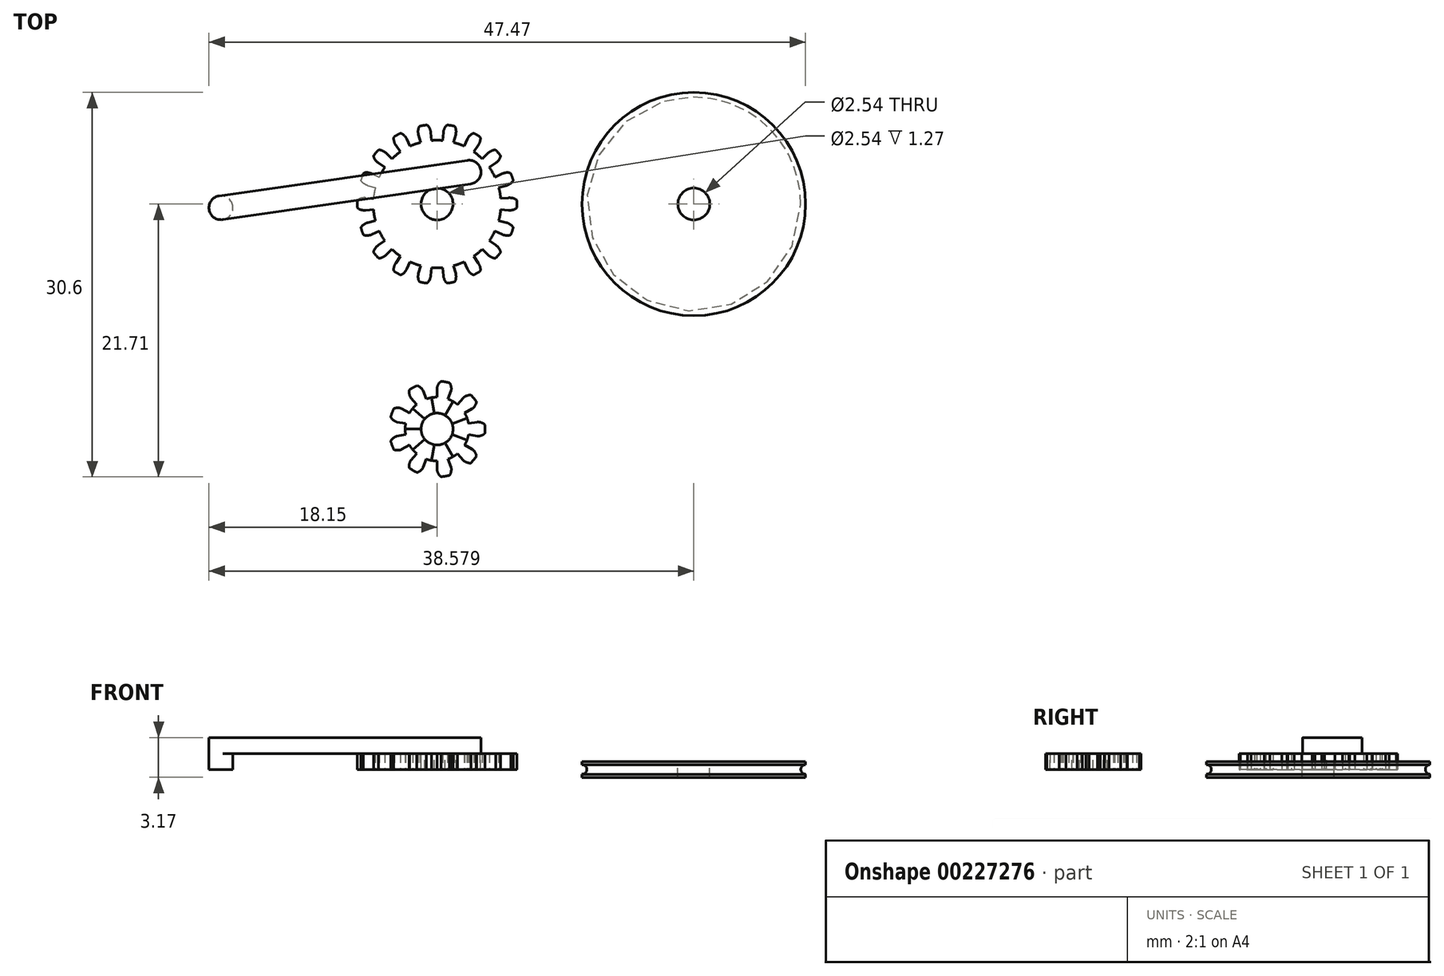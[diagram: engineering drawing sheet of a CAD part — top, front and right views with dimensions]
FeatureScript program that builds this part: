
annotation { "Feature Type Name" : "Feature", "Feature Type Description" : "" }
export const myFeature = defineFeature(function(context is Context, id is Id, definition is map)
    precondition{}
    {
        {
            var Q0;
            Q0=qCreatedBy(makeId("Top.planeOp"),FACE);
            var sketch = newSketch(context, id + "F0", { "sketchPlane" : qUnion([Q0])});
            skCircle(sketch, "E0", {"center": v(0, 0) * mm, "radius": 6.35 * mm, "construction": true});
            skCircle(sketch, "E1", {"center": v(0, 0) * mm, "radius": 5.72 * mm, "construction": true});
            skCircle(sketch, "E2", {"center": v(0, 0) * mm, "radius": 5.08 * mm, "construction": true});
            skLineSegment(sketch, "E3", {"start": v(0, 0) * mm, "end": v(7.72, 0) * mm, "construction": true});
            skLineSegment(sketch, "E4", {"start": v(0, 0) * mm, "end": v(7.94, 1.4) * mm, "construction": true});
            skLineSegment(sketch, "E5", {"start": v(0, 0) * mm, "end": v(7.47, 0.65) * mm, "construction": true});
            skLineSegment(sketch, "E6", {"start": v(0, 0) * mm, "end": v(7.02, 0.3) * mm, "construction": true});
            skFitSpline(sketch, "E7", {"points": [v(5.7, 0.5) * mm, v(6.34, 0.28) * mm], "startDerivative": vector(0.82, 0.07) * mm, "endDerivative": vector(0.13, -0.38) * mm});
            skLineSegment(sketch, "E8", {"start": v(5.7, 0.5) * mm, "end": v(5.06, 0.44) * mm});
            skPoint(sketch, "E9", {"position": v(5, 0.88) * mm});
            skArc(sketch, "E10", {"start": v(5.06, 0.44) * mm, "mid": v(5.04, 0.66) * mm, "end": v(5, 0.88) * mm});
            skArc(sketch, "E11", {"start": v(6.35, 0) * mm, "mid": v(6.35, 0.14) * mm, "end": v(6.34, 0.28) * mm});
            skPoint(sketch, "E12", {"position": v(6.35, 0) * mm});
            skLineSegment(sketch, "E13.MirrorCS", {"start": v(0, 0) * mm, "end": v(5, -0.88) * mm});
            skArc(sketch, "E14.MirrorCS", {"start": v(5.06, -0.44) * mm, "mid": v(5.04, -0.66) * mm, "end": v(5, -0.88) * mm});
            skLineSegment(sketch, "E15.MirrorCS", {"start": v(5.7, -0.5) * mm, "end": v(5.06, -0.44) * mm});
            skFitSpline(sketch, "E16.MirrorCS", {"points": [v(5.7, -0.5) * mm, v(6.34, -0.28) * mm], "startDerivative": vector(0.82, -0.07) * mm, "endDerivative": vector(0.13, 0.38) * mm});
            skArc(sketch, "E17.MirrorCS", {"start": v(6.35, 0) * mm, "mid": v(6.35, -0.14) * mm, "end": v(6.34, -0.28) * mm});
            skLineSegment(sketch, "E18", {"start": v(0, 0) * mm, "end": v(5, 0.88) * mm});
            skSolve(sketch);
        }
        {
            var Q0;
            Q0=makeQuery(id+"F0.imprint","IMPRINT",FACE,{"disambiguationData":[TD([[makeQuery(id+"F0.imprint","IMPRINT",EDGE,{"derivedFrom":sQuery(id+"F0.wireOp",EDGE,"E7")}),-1.0]])]});
            extrude(context, id + "F1", {"entities" : qUnion([Q0]), "depth" : 1.27 * mm});
        }
        {
            var Q0;
            Q0=makeQuery(id+"F1.opExtrude","SWEPT_BODY",BODY,{"disambiguationData":[OSD([sQuery(id+"F0.wireOp",EDGE,"E7"),sQuery(id+"F0.wireOp",EDGE,"E8"),sQuery(id+"F0.wireOp",EDGE,"E10"),sQuery(id+"F0.wireOp",EDGE,"E11"),sQuery(id+"F0.wireOp",EDGE,"E13.MirrorCS"),sQuery(id+"F0.wireOp",EDGE,"E14.MirrorCS"),sQuery(id+"F0.wireOp",EDGE,"E15.MirrorCS"),sQuery(id+"F0.wireOp",EDGE,"E16.MirrorCS"),sQuery(id+"F0.wireOp",EDGE,"E17.MirrorCS"),sQuery(id+"F0.wireOp",EDGE,"E18")])]});
            var Q1;
            Q1=makeQuery(id+"F1.opExtrude","SWEPT_EDGE",EDGE,{"disambiguationData":[OSD([sQuery(id+"F0.wireOp",EDGE,"E13.MirrorCS"),sQuery(id+"F0.wireOp",EDGE,"E18")])]});
            circularPattern(context, id + "F2", {"operationType" : NewBodyOperationType.ADD, "entities" : qUnion([Q0]), "axis" : qUnion([Q1]), "angle" : 360 * degree, "instanceCount" : 18, "equalSpace" : true});
        }
        {
            var Q0;
            {var subQ0=makeQuery(id+"F1.opExtrude","CAP_FACE",FACE,{"disambiguationData":[OSD([sQuery(id+"F0.wireOp",EDGE,"E7"),sQuery(id+"F0.wireOp",EDGE,"E8"),sQuery(id+"F0.wireOp",EDGE,"E10"),sQuery(id+"F0.wireOp",EDGE,"E11"),sQuery(id+"F0.wireOp",EDGE,"E13.MirrorCS"),sQuery(id+"F0.wireOp",EDGE,"E14.MirrorCS"),sQuery(id+"F0.wireOp",EDGE,"E15.MirrorCS"),sQuery(id+"F0.wireOp",EDGE,"E16.MirrorCS"),sQuery(id+"F0.wireOp",EDGE,"E17.MirrorCS"),sQuery(id+"F0.wireOp",EDGE,"E18")])],"isStart":false});Q0=makeQuery(id+"F2.boolean.opBoolean","MERGE",FACE,{"derivedFrom":[subQ0,makeQuery(id+"F2.opPattern","COPY",FACE,{"derivedFrom":subQ0,"instanceName":"1"}),makeQuery(id+"F2.opPattern","COPY",FACE,{"derivedFrom":subQ0,"instanceName":"2"}),makeQuery(id+"F2.opPattern","COPY",FACE,{"derivedFrom":subQ0,"instanceName":"3"}),makeQuery(id+"F2.opPattern","COPY",FACE,{"derivedFrom":subQ0,"instanceName":"4"}),makeQuery(id+"F2.opPattern","COPY",FACE,{"derivedFrom":subQ0,"instanceName":"5"}),makeQuery(id+"F2.opPattern","COPY",FACE,{"derivedFrom":subQ0,"instanceName":"6"}),makeQuery(id+"F2.opPattern","COPY",FACE,{"derivedFrom":subQ0,"instanceName":"7"}),makeQuery(id+"F2.opPattern","COPY",FACE,{"derivedFrom":subQ0,"instanceName":"8"}),makeQuery(id+"F2.opPattern","COPY",FACE,{"derivedFrom":subQ0,"instanceName":"9"}),makeQuery(id+"F2.opPattern","COPY",FACE,{"derivedFrom":subQ0,"instanceName":"10"}),makeQuery(id+"F2.opPattern","COPY",FACE,{"derivedFrom":subQ0,"instanceName":"11"}),makeQuery(id+"F2.opPattern","COPY",FACE,{"derivedFrom":subQ0,"instanceName":"12"}),makeQuery(id+"F2.opPattern","COPY",FACE,{"derivedFrom":subQ0,"instanceName":"13"}),makeQuery(id+"F2.opPattern","COPY",FACE,{"derivedFrom":subQ0,"instanceName":"14"}),makeQuery(id+"F2.opPattern","COPY",FACE,{"derivedFrom":subQ0,"instanceName":"15"}),makeQuery(id+"F2.opPattern","COPY",FACE,{"derivedFrom":subQ0,"instanceName":"16"}),makeQuery(id+"F2.opPattern","COPY",FACE,{"derivedFrom":subQ0,"instanceName":"17"})]});}
            var sketch = newSketch(context, id + "F3", { "sketchPlane" : qUnion([Q0])});
            skCircle(sketch, "E19", {"center": v(2.54, 2.54) * mm, "radius": 0.95 * mm});
            skPoint(sketch, "E20.0", {"position": v(0, 0) * mm});
            skSolve(sketch);
        }
        {
            var Q0;
            Q0=makeQuery(id+"F3.imprint","IMPRINT",FACE,{"disambiguationData":[TD([[makeQuery(id+"F3.imprint","IMPRINT",EDGE,{"derivedFrom":sQuery(id+"F3.wireOp",EDGE,"E19")}),1.0]])]});
            extrude(context, id + "F4", {"entities" : qUnion([Q0]), "operationType" : NewBodyOperationType.REMOVE, "oppositeDirection" : true, "depth" : 25.4 * mm});
        }
        {
            var Q0;
            {var subQ0=makeQuery(id+"F1.opExtrude","CAP_FACE",FACE,{"disambiguationData":[OSD([sQuery(id+"F0.wireOp",EDGE,"E7"),sQuery(id+"F0.wireOp",EDGE,"E8"),sQuery(id+"F0.wireOp",EDGE,"E10"),sQuery(id+"F0.wireOp",EDGE,"E11"),sQuery(id+"F0.wireOp",EDGE,"E13.MirrorCS"),sQuery(id+"F0.wireOp",EDGE,"E14.MirrorCS"),sQuery(id+"F0.wireOp",EDGE,"E15.MirrorCS"),sQuery(id+"F0.wireOp",EDGE,"E16.MirrorCS"),sQuery(id+"F0.wireOp",EDGE,"E17.MirrorCS"),sQuery(id+"F0.wireOp",EDGE,"E18")])],"isStart":false});Q0=makeQuery(id+"F2.boolean.opBoolean","MERGE",FACE,{"derivedFrom":[subQ0,makeQuery(id+"F2.opPattern","COPY",FACE,{"derivedFrom":subQ0,"instanceName":"1"}),makeQuery(id+"F2.opPattern","COPY",FACE,{"derivedFrom":subQ0,"instanceName":"2"}),makeQuery(id+"F2.opPattern","COPY",FACE,{"derivedFrom":subQ0,"instanceName":"3"}),makeQuery(id+"F2.opPattern","COPY",FACE,{"derivedFrom":subQ0,"instanceName":"4"}),makeQuery(id+"F2.opPattern","COPY",FACE,{"derivedFrom":subQ0,"instanceName":"5"}),makeQuery(id+"F2.opPattern","COPY",FACE,{"derivedFrom":subQ0,"instanceName":"6"}),makeQuery(id+"F2.opPattern","COPY",FACE,{"derivedFrom":subQ0,"instanceName":"7"}),makeQuery(id+"F2.opPattern","COPY",FACE,{"derivedFrom":subQ0,"instanceName":"8"}),makeQuery(id+"F2.opPattern","COPY",FACE,{"derivedFrom":subQ0,"instanceName":"9"}),makeQuery(id+"F2.opPattern","COPY",FACE,{"derivedFrom":subQ0,"instanceName":"10"}),makeQuery(id+"F2.opPattern","COPY",FACE,{"derivedFrom":subQ0,"instanceName":"11"}),makeQuery(id+"F2.opPattern","COPY",FACE,{"derivedFrom":subQ0,"instanceName":"12"}),makeQuery(id+"F2.opPattern","COPY",FACE,{"derivedFrom":subQ0,"instanceName":"13"}),makeQuery(id+"F2.opPattern","COPY",FACE,{"derivedFrom":subQ0,"instanceName":"14"}),makeQuery(id+"F2.opPattern","COPY",FACE,{"derivedFrom":subQ0,"instanceName":"15"}),makeQuery(id+"F2.opPattern","COPY",FACE,{"derivedFrom":subQ0,"instanceName":"16"}),makeQuery(id+"F2.opPattern","COPY",FACE,{"derivedFrom":subQ0,"instanceName":"17"})]});}
            var sketch = newSketch(context, id + "F5", { "sketchPlane" : qUnion([Q0])});
            skPoint(sketch, "E21.0", {"position": v(0, 0) * mm});
            skCircle(sketch, "E22", {"center": v(0, 0) * mm, "radius": 1.27 * mm});
            skSolve(sketch);
        }
        {
            var Q0;
            Q0=makeQuery(id+"F5.imprint","IMPRINT",FACE,{"disambiguationData":[TD([[makeQuery(id+"F5.imprint","IMPRINT",EDGE,{"derivedFrom":sQuery(id+"F5.wireOp",EDGE,"E22")}),1.0]])]});
            extrude(context, id + "F6", {"entities" : qUnion([Q0]), "operationType" : NewBodyOperationType.REMOVE, "oppositeDirection" : true, "depth" : 25.4 * mm});
        }
        {
            var Q0;
            Q0=qCreatedBy(makeId("Top.planeOp"),FACE);
            var sketch = newSketch(context, id + "F7", { "sketchPlane" : qUnion([Q0])});
            skCircle(sketch, "E23", {"center": v(20.43, 6.42) * mm, "radius": 6.35 * mm});
            skCircle(sketch, "E24", {"center": v(20.43, 6.42) * mm, "radius": 1.27 * mm});
            skSolve(sketch);
        }
        {
            var Q0;
            Q0=qCreatedBy(makeId("Front.planeOp"),FACE);
            var sketch = newSketch(context, id + "F8", { "sketchPlane" : qUnion([Q0])});
            skPoint(sketch, "E25.0", {"position": v(20.43, 0) * mm});
            skLineSegment(sketch, "E26", {"start": v(29.32, 0.38) * mm, "end": v(29.32, 0.64) * mm});
            skLineSegment(sketch, "E27", {"start": v(29.32, 0.64) * mm, "end": v(20.43, 0.64) * mm});
            skLineSegment(sketch, "E28", {"start": v(20.43, 0.64) * mm, "end": v(20.43, 0) * mm});
            skLineSegment(sketch, "E29", {"start": v(20.43, 0) * mm, "end": v(20.43, -0.63) * mm});
            skLineSegment(sketch, "E30", {"start": v(20.43, -0.63) * mm, "end": v(29.32, -0.63) * mm});
            skLineSegment(sketch, "E31", {"start": v(29.32, -0.63) * mm, "end": v(29.32, -0.38) * mm});
            skArc(sketch, "E32", {"start": v(29.32, 0.38) * mm, "mid": v(28.94, 0) * mm, "end": v(29.32, -0.38) * mm});
            skLineSegment(sketch, "E33", {"start": v(29.32, -0.38) * mm, "end": v(29.32, 0.38) * mm});
            skSolve(sketch);
        }
        {
            var Q0;
            Q0=qCreatedBy(makeId("Top.planeOp"),FACE);
            var sketch = newSketch(context, id + "F9", { "sketchPlane" : qUnion([Q0])});
            skArc(sketch, "E34", {"start": v(3.81, -17.9) * mm, "mid": v(3.8, -17.58) * mm, "end": v(3.75, -17.25) * mm, "construction": true});
            skArc(sketch, "E35", {"start": v(2.5, -17.47) * mm, "mid": v(2.45, -17.25) * mm, "end": v(2.39, -17.04) * mm, "construction": true});
            skLineSegment(sketch, "E36", {"start": v(0, -17.9) * mm, "end": v(3.81, -17.9) * mm, "construction": true});
            skLineSegment(sketch, "E37", {"start": v(0, -17.9) * mm, "end": v(2.39, -17.04) * mm, "construction": true});
            skLineSegment(sketch, "E38", {"start": v(0, -17.9) * mm, "end": v(3.2, -17.35) * mm, "construction": true});
            skLineSegment(sketch, "E39", {"start": v(0, -17.9) * mm, "end": v(3.8, -17.58) * mm, "construction": true});
            skLineSegment(sketch, "E40", {"start": v(0, -17.9) * mm, "end": v(2.39, -17.04) * mm});
            skLineSegment(sketch, "E41", {"start": v(2.5, -17.47) * mm, "end": v(3.2, -17.35) * mm});
            skArc(sketch, "E42", {"start": v(2.5, -17.47) * mm, "mid": v(2.45, -17.25) * mm, "end": v(2.39, -17.04) * mm});
            skLineSegment(sketch, "E43", {"start": v(0, -17.9) * mm, "end": v(3.81, -17.9) * mm});
            skFitSpline(sketch, "E44", {"points": [v(3.2, -17.35) * mm, v(3.8, -17.58) * mm], "startDerivative": vector(0.63, 0.11) * mm, "endDerivative": vector(0.02, -0.25) * mm});
            skArc(sketch, "E45", {"start": v(3.81, -17.9) * mm, "mid": v(3.8, -17.58) * mm, "end": v(3.75, -17.25) * mm});
            skLineSegment(sketch, "E46.MirrorCS", {"start": v(0, -17.9) * mm, "end": v(2.39, -18.78) * mm});
            skArc(sketch, "E47.MirrorCS", {"start": v(2.5, -18.35) * mm, "mid": v(2.45, -18.57) * mm, "end": v(2.39, -18.78) * mm});
            skLineSegment(sketch, "E48.MirrorCS", {"start": v(2.5, -18.35) * mm, "end": v(3.2, -18.47) * mm});
            skFitSpline(sketch, "E49.MirrorCS", {"points": [v(3.2, -18.47) * mm, v(3.8, -18.24) * mm], "startDerivative": vector(0.63, -0.11) * mm, "endDerivative": vector(0.02, 0.25) * mm});
            skArc(sketch, "E50.MirrorCS", {"start": v(3.81, -17.9) * mm, "mid": v(3.8, -18.24) * mm, "end": v(3.75, -18.57) * mm});
            skSolve(sketch);
        }
        {
            var Q0;
            {var subQ0=sQuery(id+"F9.wireOp",EDGE,"E43");Q0=makeQuery(id+"F9.imprint","IMPRINT",FACE,{"disambiguationData":[TD([[makeQuery(id+"F9.imprint","IMPRINT",EDGE,{"derivedFrom":subQ0}),-1.0]])]});}
            var Q1;
            Q1=makeQuery(id+"F9.imprint","IMPRINT",FACE,{"disambiguationData":[TD([[makeQuery(id+"F9.imprint","IMPRINT",EDGE,{"derivedFrom":sQuery(id+"F9.wireOp",EDGE,"E40")}),-1.0]])]});
            extrude(context, id + "F10", {"entities" : qUnion([Q0, Q1]), "depth" : 1.27 * mm});
        }
        {
            var Q0;
            Q0=makeQuery(id+"F10.opExtrude","SWEPT_BODY",BODY,{"disambiguationData":[OSD([sQuery(id+"F9.wireOp",EDGE,"E40"),sQuery(id+"F9.wireOp",EDGE,"E41"),sQuery(id+"F9.wireOp",EDGE,"E42"),sQuery(id+"F9.wireOp",EDGE,"E44"),sQuery(id+"F9.wireOp",EDGE,"E45"),sQuery(id+"F9.wireOp",EDGE,"E46.MirrorCS"),sQuery(id+"F9.wireOp",EDGE,"E47.MirrorCS"),sQuery(id+"F9.wireOp",EDGE,"E48.MirrorCS"),sQuery(id+"F9.wireOp",EDGE,"E49.MirrorCS"),sQuery(id+"F9.wireOp",EDGE,"E50.MirrorCS")])]});
            var Q1;
            Q1=makeQuery(id+"F10.opExtrude","SWEPT_EDGE",EDGE,{"disambiguationData":[OSD([sQuery(id+"F9.wireOp",EDGE,"E40"),sQuery(id+"F9.wireOp",EDGE,"E43"),sQuery(id+"F9.wireOp",EDGE,"E46.MirrorCS")])]});
            circularPattern(context, id + "F11", {"operationType" : NewBodyOperationType.ADD, "entities" : qUnion([Q0]), "axis" : qUnion([Q1]), "angle" : 360 * degree, "instanceCount" : 9, "equalSpace" : true});
        }
        {
            var Q0;
            {var subQ0=makeQuery(id+"F10.opExtrude","CAP_FACE",FACE,{"disambiguationData":[OSD([sQuery(id+"F9.wireOp",EDGE,"E40"),sQuery(id+"F9.wireOp",EDGE,"E41"),sQuery(id+"F9.wireOp",EDGE,"E42"),sQuery(id+"F9.wireOp",EDGE,"E44"),sQuery(id+"F9.wireOp",EDGE,"E45"),sQuery(id+"F9.wireOp",EDGE,"E46.MirrorCS"),sQuery(id+"F9.wireOp",EDGE,"E47.MirrorCS"),sQuery(id+"F9.wireOp",EDGE,"E48.MirrorCS"),sQuery(id+"F9.wireOp",EDGE,"E49.MirrorCS"),sQuery(id+"F9.wireOp",EDGE,"E50.MirrorCS")])],"isStart":false});Q0=makeQuery(id+"F11.boolean.opBoolean","MERGE",FACE,{"derivedFrom":[subQ0,makeQuery(id+"F11.opPattern","COPY",FACE,{"derivedFrom":subQ0,"instanceName":"1"}),makeQuery(id+"F11.opPattern","COPY",FACE,{"derivedFrom":subQ0,"instanceName":"2"}),makeQuery(id+"F11.opPattern","COPY",FACE,{"derivedFrom":subQ0,"instanceName":"3"}),makeQuery(id+"F11.opPattern","COPY",FACE,{"derivedFrom":subQ0,"instanceName":"4"}),makeQuery(id+"F11.opPattern","COPY",FACE,{"derivedFrom":subQ0,"instanceName":"5"}),makeQuery(id+"F11.opPattern","COPY",FACE,{"derivedFrom":subQ0,"instanceName":"6"}),makeQuery(id+"F11.opPattern","COPY",FACE,{"derivedFrom":subQ0,"instanceName":"7"}),makeQuery(id+"F11.opPattern","COPY",FACE,{"derivedFrom":subQ0,"instanceName":"8"})]});}
            var sketch = newSketch(context, id + "F12", { "sketchPlane" : qUnion([Q0])});
            skCircle(sketch, "E51", {"center": v(0, -17.9) * mm, "radius": 1.27 * mm});
            skArc(sketch, "E52.0", {"start": v(2.5, -18.35) * mm, "mid": v(2.39, -18.78) * mm, "end": v(2.2, -19.18) * mm});
            skSolve(sketch);
        }
        {
            var Q0;
            Q0=makeQuery(id+"F12.imprint","IMPRINT",FACE,{"disambiguationData":[TD([[makeQuery(id+"F12.imprint","IMPRINT",EDGE,{"derivedFrom":sQuery(id+"F12.wireOp",EDGE,"E51")}),1.0]])]});
            extrude(context, id + "F13", {"entities" : qUnion([Q0]), "operationType" : NewBodyOperationType.REMOVE, "oppositeDirection" : true, "depth" : 25.4 * mm});
        }
        {
            var Q0;
            {var subQ0=makeQuery(id+"F1.opExtrude","CAP_FACE",FACE,{"disambiguationData":[OSD([sQuery(id+"F0.wireOp",EDGE,"E7"),sQuery(id+"F0.wireOp",EDGE,"E8"),sQuery(id+"F0.wireOp",EDGE,"E10"),sQuery(id+"F0.wireOp",EDGE,"E11"),sQuery(id+"F0.wireOp",EDGE,"E13.MirrorCS"),sQuery(id+"F0.wireOp",EDGE,"E14.MirrorCS"),sQuery(id+"F0.wireOp",EDGE,"E15.MirrorCS"),sQuery(id+"F0.wireOp",EDGE,"E16.MirrorCS"),sQuery(id+"F0.wireOp",EDGE,"E17.MirrorCS"),sQuery(id+"F0.wireOp",EDGE,"E18")])],"isStart":true});Q0=makeQuery(id+"F2.boolean.opBoolean","MERGE",FACE,{"derivedFrom":[subQ0,makeQuery(id+"F2.opPattern","COPY",FACE,{"derivedFrom":subQ0,"instanceName":"1"}),makeQuery(id+"F2.opPattern","COPY",FACE,{"derivedFrom":subQ0,"instanceName":"2"}),makeQuery(id+"F2.opPattern","COPY",FACE,{"derivedFrom":subQ0,"instanceName":"3"}),makeQuery(id+"F2.opPattern","COPY",FACE,{"derivedFrom":subQ0,"instanceName":"4"}),makeQuery(id+"F2.opPattern","COPY",FACE,{"derivedFrom":subQ0,"instanceName":"5"}),makeQuery(id+"F2.opPattern","COPY",FACE,{"derivedFrom":subQ0,"instanceName":"6"}),makeQuery(id+"F2.opPattern","COPY",FACE,{"derivedFrom":subQ0,"instanceName":"7"}),makeQuery(id+"F2.opPattern","COPY",FACE,{"derivedFrom":subQ0,"instanceName":"8"}),makeQuery(id+"F2.opPattern","COPY",FACE,{"derivedFrom":subQ0,"instanceName":"9"}),makeQuery(id+"F2.opPattern","COPY",FACE,{"derivedFrom":subQ0,"instanceName":"10"}),makeQuery(id+"F2.opPattern","COPY",FACE,{"derivedFrom":subQ0,"instanceName":"11"}),makeQuery(id+"F2.opPattern","COPY",FACE,{"derivedFrom":subQ0,"instanceName":"12"}),makeQuery(id+"F2.opPattern","COPY",FACE,{"derivedFrom":subQ0,"instanceName":"13"}),makeQuery(id+"F2.opPattern","COPY",FACE,{"derivedFrom":subQ0,"instanceName":"14"}),makeQuery(id+"F2.opPattern","COPY",FACE,{"derivedFrom":subQ0,"instanceName":"15"}),makeQuery(id+"F2.opPattern","COPY",FACE,{"derivedFrom":subQ0,"instanceName":"16"}),makeQuery(id+"F2.opPattern","COPY",FACE,{"derivedFrom":subQ0,"instanceName":"17"})]});}
            var sketch = newSketch(context, id + "F14", { "sketchPlane" : qUnion([Q0])});
            skCircle(sketch, "E53.0", {"center": v(2.54, -2.54) * mm, "radius": 0.95 * mm});
            skSolve(sketch);
        }
        {
            var Q0;
            Q0=makeQuery(id+"F14.imprint","IMPRINT",FACE,{"disambiguationData":[TD([[makeQuery(id+"F14.imprint","IMPRINT",EDGE,{"derivedFrom":sQuery(id+"F14.wireOp",EDGE,"E53.0")}),-1.0]])]});
            extrude(context, id + "F15", {"entities" : qUnion([Q0]), "oppositeDirection" : true, "depth" : 2.54 * mm});
        }
        {
            var Q0;
            Q0=makeQuery(id+"F15.opExtrude","CAP_FACE",FACE,{"disambiguationData":[OSD([sQuery(id+"F14.wireOp",EDGE,"E53.0")])],"isStart":false});
            var sketch = newSketch(context, id + "F16", { "sketchPlane" : qUnion([Q0])});
            skLineSegment(sketch, "E54", {"start": v(2.4, 3.48) * mm, "end": v(-17.33, 0.65) * mm});
            skLineSegment(sketch, "E55", {"start": v(-17.33, 0.65) * mm, "end": v(-17.06, -1.24) * mm});
            skLineSegment(sketch, "E56", {"start": v(-17.06, -1.24) * mm, "end": v(2.68, 1.6) * mm});
            skCircle(sketch, "E57.0.0", {"center": v(2.54, 2.54) * mm, "radius": 0.95 * mm});
            skLineSegment(sketch, "E58", {"start": v(2.4, 3.48) * mm, "end": v(2.68, 1.6) * mm});
            skSolve(sketch);
        }
        {
            var Q0;
            {var subQ0=sQuery(id+"F16.wireOp",EDGE,"E54");Q0=makeQuery(id+"F16.imprint","IMPRINT",FACE,{"disambiguationData":[TD([[makeQuery(id+"F16.imprint","IMPRINT",EDGE,{"derivedFrom":subQ0}),1.0]])]});}
            extrude(context, id + "F17", {"entities" : qUnion([Q0]), "operationType" : NewBodyOperationType.ADD, "oppositeDirection" : true, "depth" : 1.27 * mm});
        }
        {
            var Q0;
            Q0=makeQuery(id+"F8.imprint","IMPRINT",FACE,{"disambiguationData":[TD([[makeQuery(id+"F8.imprint","IMPRINT",EDGE,{"derivedFrom":sQuery(id+"F8.wireOp",EDGE,"E26")}),1.0]])]});
            var Q1;
            Q1=sQuery(id+"F8.wireOp",EDGE,"E29");
            revolve(context, id + "F18", {"entities" : qUnion([Q0]), "axis" : qUnion([Q1]), "revolveType" : RevolveType.FULL});
        }
        {
            var Q0;
            Q0=makeQuery(id+"F18.opRevolve","SWEPT_FACE",FACE,{"disambiguationData":[OSD([sQuery(id+"F8.wireOp",EDGE,"E27")])]});
            var sketch = newSketch(context, id + "F19", { "sketchPlane" : qUnion([Q0])});
            skCircle(sketch, "E59.0.0", {"center": v(20.43, 0) * mm, "radius": 8.9 * mm});
            skCircle(sketch, "E60", {"center": v(20.43, 0) * mm, "radius": 1.27 * mm});
            skSolve(sketch);
        }
        {
            var Q0;
            Q0=makeQuery(id+"F19.imprint","IMPRINT",FACE,{"disambiguationData":[TD([[makeQuery(id+"F19.imprint","IMPRINT",EDGE,{"derivedFrom":sQuery(id+"F19.wireOp",EDGE,"E60")}),1.0]])]});
            extrude(context, id + "F20", {"entities" : qUnion([Q0]), "operationType" : NewBodyOperationType.REMOVE, "oppositeDirection" : true, "depth" : 14 * mm});
        }
        {
            var Q0;
            Q0=makeQuery(id+"F17.boolean.opBoolean","MERGE",FACE,{"derivedFrom":[makeQuery(id+"F15.opExtrude","CAP_FACE",FACE,{"disambiguationData":[OSD([sQuery(id+"F14.wireOp",EDGE,"E53.0")])],"isStart":false}),makeQuery(id+"F17.opExtrude","CAP_FACE",FACE,{"disambiguationData":[OSD([sQuery(id+"F16.wireOp",EDGE,"E54"),sQuery(id+"F16.wireOp",EDGE,"E55"),sQuery(id+"F16.wireOp",EDGE,"E56"),sQuery(id+"F16.wireOp",EDGE,"E57.0.0")])],"isStart":true})]});
            var sketch = newSketch(context, id + "F21", { "sketchPlane" : qUnion([Q0])});
            skPoint(sketch, "E61.0", {"position": v(-17.2, -0.3) * mm});
            skPoint(sketch, "E62.0", {"position": v(-17.33, 0.65) * mm});
            skCircle(sketch, "E63", {"center": v(-17.2, -0.3) * mm, "radius": 0.95 * mm});
            skSolve(sketch);
        }
        {
            var Q0;
            {var subQ1=makeQuery(id+"F17.opExtrude","CAP_EDGE",EDGE,{"disambiguationData":[OSD([sQuery(id+"F16.wireOp",EDGE,"E55")])],"isStart":true});Q0=makeQuery(id+"F21.imprint","IMPRINT",FACE,{"disambiguationData":[TD([[makeQuery(id+"F21.imprint","IMPRINT",EDGE,{"derivedFrom":subQ1}),-1.0]])]});}
            var Q1;
            {var subQ1=makeQuery(id+"F17.opExtrude","CAP_EDGE",EDGE,{"disambiguationData":[OSD([sQuery(id+"F16.wireOp",EDGE,"E55")])],"isStart":true});Q1=makeQuery(id+"F21.imprint","IMPRINT",FACE,{"disambiguationData":[TD([[makeQuery(id+"F21.imprint","IMPRINT",EDGE,{"derivedFrom":subQ1}),1.0]])]});}
            extrude(context, id + "F22", {"entities" : qUnion([Q0, Q1]), "operationType" : NewBodyOperationType.ADD, "oppositeDirection" : true, "depth" : 2.54 * mm});
        }
    });
